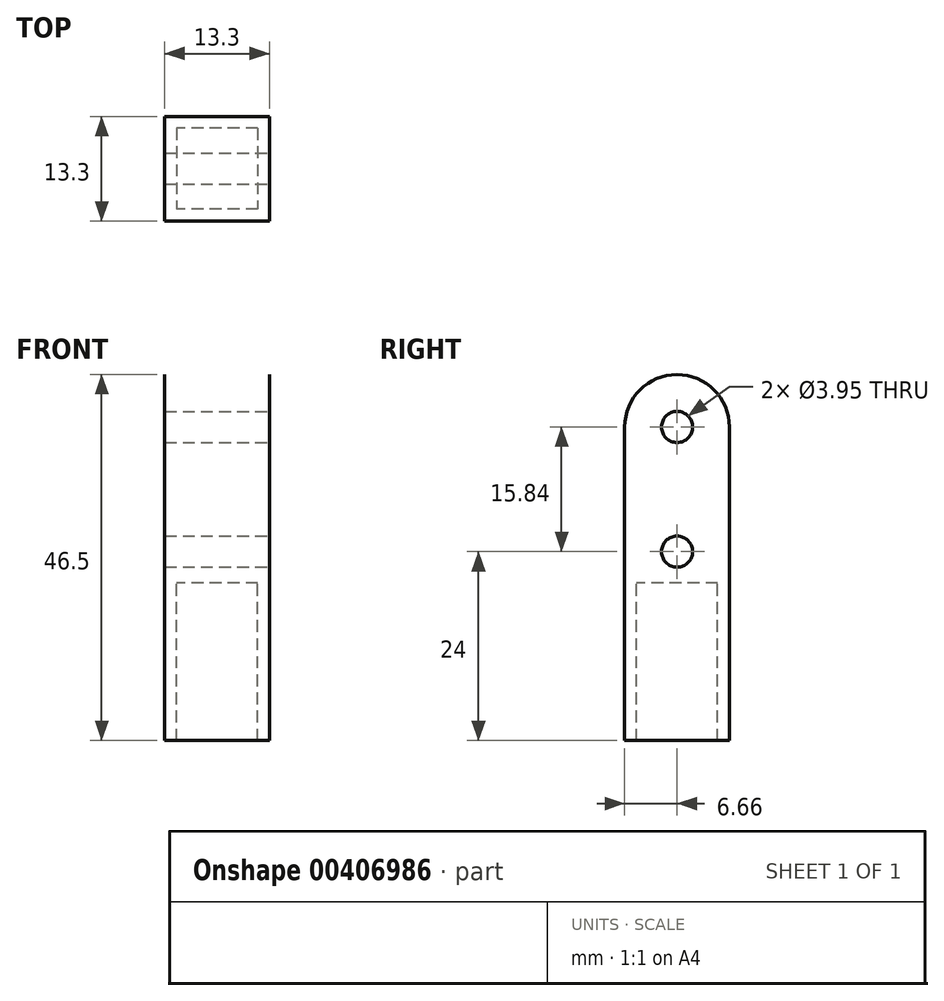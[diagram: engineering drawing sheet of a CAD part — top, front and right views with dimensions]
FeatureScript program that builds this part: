
annotation { "Feature Type Name" : "Feature", "Feature Type Description" : "" }
export const myFeature = defineFeature(function(context is Context, id is Id, definition is map)
    precondition{}
    {
        {
            var Q0;
            Q0=qCreatedBy(makeId("Top.planeOp"),FACE);
            var sketch = newSketch(context, id + "F0", { "sketchPlane" : qUnion([Q0])});
            skLineSegment(sketch, "E0.bottom", {"start": v(5.15, 5.15) * mm, "end": v(-5.15, 5.15) * mm});
            skLineSegment(sketch, "E0.top", {"start": v(5.15, -5.15) * mm, "end": v(-5.15, -5.15) * mm});
            skLineSegment(sketch, "E0.left", {"start": v(5.15, 5.15) * mm, "end": v(5.15, -5.15) * mm});
            skLineSegment(sketch, "E0.right", {"start": v(-5.15, 5.15) * mm, "end": v(-5.15, -5.15) * mm});
            skPoint(sketch, "E0.middle", {"position": v(0, 0) * mm});
            skLineSegment(sketch, "E1.bottom", {"start": v(6.65, 6.65) * mm, "end": v(-6.65, 6.65) * mm});
            skLineSegment(sketch, "E1.top", {"start": v(6.65, -6.65) * mm, "end": v(-6.65, -6.65) * mm});
            skLineSegment(sketch, "E1.left", {"start": v(6.65, 6.65) * mm, "end": v(6.65, -6.65) * mm});
            skLineSegment(sketch, "E1.right", {"start": v(-6.65, 6.65) * mm, "end": v(-6.65, -6.65) * mm});
            skSolve(sketch);
        }
        {
            var Q0;
            Q0=makeQuery(id+"F0.imprint","IMPRINT",FACE,{"disambiguationData":[TD([[makeQuery(id+"F0.imprint","IMPRINT",EDGE,{"derivedFrom":sQuery(id+"F0.wireOp",EDGE,"E0.bottom")}),-1.0]])]});
            extrude(context, id + "F1", {"entities" : qUnion([Q0]), "oppositeDirection" : true, "depth" : 20 * mm});
        }
        {
            var Q0;
            Q0=makeQuery(id+"F0.imprint","IMPRINT",FACE,{"disambiguationData":[TD([[makeQuery(id+"F0.imprint","IMPRINT",EDGE,{"derivedFrom":sQuery(id+"F0.wireOp",EDGE,"E0.bottom")}),1.0]])]});
            var Q1;
            Q1=makeQuery(id+"F0.imprint","IMPRINT",FACE,{"disambiguationData":[TD([[makeQuery(id+"F0.imprint","IMPRINT",EDGE,{"derivedFrom":sQuery(id+"F0.wireOp",EDGE,"E0.bottom")}),-1.0]])]});
            extrude(context, id + "F2", {"entities" : qUnion([Q0, Q1]), "operationType" : NewBodyOperationType.ADD, "depth" : 1.5 * mm});
        }
        {
            var Q0;
            Q0=makeQuery(id+"F2.opExtrude","CAP_FACE",FACE,{"disambiguationData":[OSD([sQuery(id+"F0.wireOp",EDGE,"E1.bottom"),sQuery(id+"F0.wireOp",EDGE,"E1.top"),sQuery(id+"F0.wireOp",EDGE,"E1.left"),sQuery(id+"F0.wireOp",EDGE,"E1.right")])],"isStart":false});
            var sketch = newSketch(context, id + "F3", { "sketchPlane" : qUnion([Q0])});
            skLineSegment(sketch, "E2.bottom", {"start": v(-6.65, -6.65) * mm, "end": v(-2.65, -6.65) * mm});
            skLineSegment(sketch, "E2.top", {"start": v(-6.65, 6.65) * mm, "end": v(-2.65, 6.65) * mm});
            skLineSegment(sketch, "E2.left", {"start": v(-6.65, -6.65) * mm, "end": v(-6.65, 6.65) * mm});
            skLineSegment(sketch, "E2.right", {"start": v(-2.65, -6.65) * mm, "end": v(-2.65, 6.65) * mm});
            skLineSegment(sketch, "E3.MirrorCS", {"start": v(2.65, -6.65) * mm, "end": v(2.65, 6.65) * mm});
            skLineSegment(sketch, "E4.MirrorCS", {"start": v(6.65, 6.65) * mm, "end": v(2.65, 6.65) * mm});
            skLineSegment(sketch, "E5.MirrorCS", {"start": v(6.65, -6.65) * mm, "end": v(6.65, 6.65) * mm});
            skLineSegment(sketch, "E6.MirrorCS", {"start": v(6.65, -6.65) * mm, "end": v(2.65, -6.65) * mm});
            skSolve(sketch);
        }
        {
            var Q0;
            Q0=makeQuery(id+"F3.imprint","IMPRINT",FACE,{"disambiguationData":[TD([[makeQuery(id+"F3.imprint","IMPRINT",EDGE,{"derivedFrom":sQuery(id+"F3.wireOp",EDGE,"E2.bottom")}),-1.0]])]});
            var Q1;
            Q1=makeQuery(id+"F3.imprint","IMPRINT",FACE,{"disambiguationData":[TD([[makeQuery(id+"F3.imprint","IMPRINT",EDGE,{"derivedFrom":sQuery(id+"F3.wireOp",EDGE,"E3.MirrorCS")}),-1.0]])]});
            var Q2;
            {var subQ0=sQuery(id+"F3.wireOp",EDGE,"E2.right");Q2=makeQuery(id+"F3.imprint","IMPRINT",FACE,{"disambiguationData":[TD([[makeQuery(id+"F3.imprint","IMPRINT",EDGE,{"derivedFrom":subQ0}),-1.0]])]});}
            extrude(context, id + "F4", {"entities" : qUnion([Q0, Q1, Q2]), "operationType" : NewBodyOperationType.ADD, "depth" : 25 * mm});
        }
        {
            var Q0;
            Q0=makeQuery(id+"F4.opExtrude","CAP_EDGE",EDGE,{"disambiguationData":[OSD([sQuery(id+"F3.wireOp",EDGE,"E4.MirrorCS")])],"isStart":false});
            var Q1;
            Q1=makeQuery(id+"F4.opExtrude","CAP_EDGE",EDGE,{"disambiguationData":[OSD([sQuery(id+"F3.wireOp",EDGE,"E6.MirrorCS")])],"isStart":false});
            var Q2;
            Q2=makeQuery(id+"F4.opExtrude","CAP_EDGE",EDGE,{"disambiguationData":[OSD([sQuery(id+"F3.wireOp",EDGE,"E2.top")])],"isStart":false});
            var Q3;
            Q3=makeQuery(id+"F4.opExtrude","CAP_EDGE",EDGE,{"disambiguationData":[OSD([sQuery(id+"F3.wireOp",EDGE,"E2.bottom")])],"isStart":false});
            fillet(context, id + "F5", {"entities" : qUnion([Q0, Q1, Q2, Q3]), "radius" : 6.66 * mm, "tangentPropagation" : true, "allowEdgeOverflow" : false});
        }
        {
            var Q0;
            {var subQ0=sQuery(id+"F0.wireOp",EDGE,"E1.left");Q0=makeQuery(id+"F4.boolean.opBoolean","MERGE",FACE,{"derivedFrom":[makeQuery(id+"F2.boolean.opBoolean","MERGE",FACE,{"derivedFrom":[makeQuery(id+"F1.opExtrude","SWEPT_FACE",FACE,{"disambiguationData":[OSD([subQ0])]}),makeQuery(id+"F2.opExtrude","SWEPT_FACE",FACE,{"disambiguationData":[OSD([subQ0])]})]}),makeQuery(id+"F4.opExtrude","SWEPT_FACE",FACE,{"disambiguationData":[OSD([sQuery(id+"F3.wireOp",EDGE,"E5.MirrorCS")])]})]});}
            var sketch = newSketch(context, id + "F6", { "sketchPlane" : qUnion([Q0])});
            skCircle(sketch, "E7", {"center": v(0.01, 4) * mm, "radius": 1.98 * mm});
            skCircle(sketch, "E8", {"center": v(0.01, 19.84) * mm, "radius": 1.98 * mm});
            skSolve(sketch);
        }
        {
            var Q0;
            Q0=makeQuery(id+"F6.imprint","IMPRINT",FACE,{"disambiguationData":[TD([[makeQuery(id+"F6.imprint","IMPRINT",EDGE,{"derivedFrom":sQuery(id+"F6.wireOp",EDGE,"E7")}),1.0]])]});
            var Q1;
            Q1=makeQuery(id+"F6.imprint","IMPRINT",FACE,{"disambiguationData":[TD([[makeQuery(id+"F6.imprint","IMPRINT",EDGE,{"derivedFrom":sQuery(id+"F6.wireOp",EDGE,"E8")}),1.0]])]});
            extrude(context, id + "F7", {"entities" : qUnion([Q0, Q1]), "operationType" : NewBodyOperationType.REMOVE, "oppositeDirection" : true, "depth" : 25 * mm, "hasSecondDirection" : true, "secondDirectionOppositeDirection" : false, "secondDirectionDepth" : 25 * mm});
        }
    });
